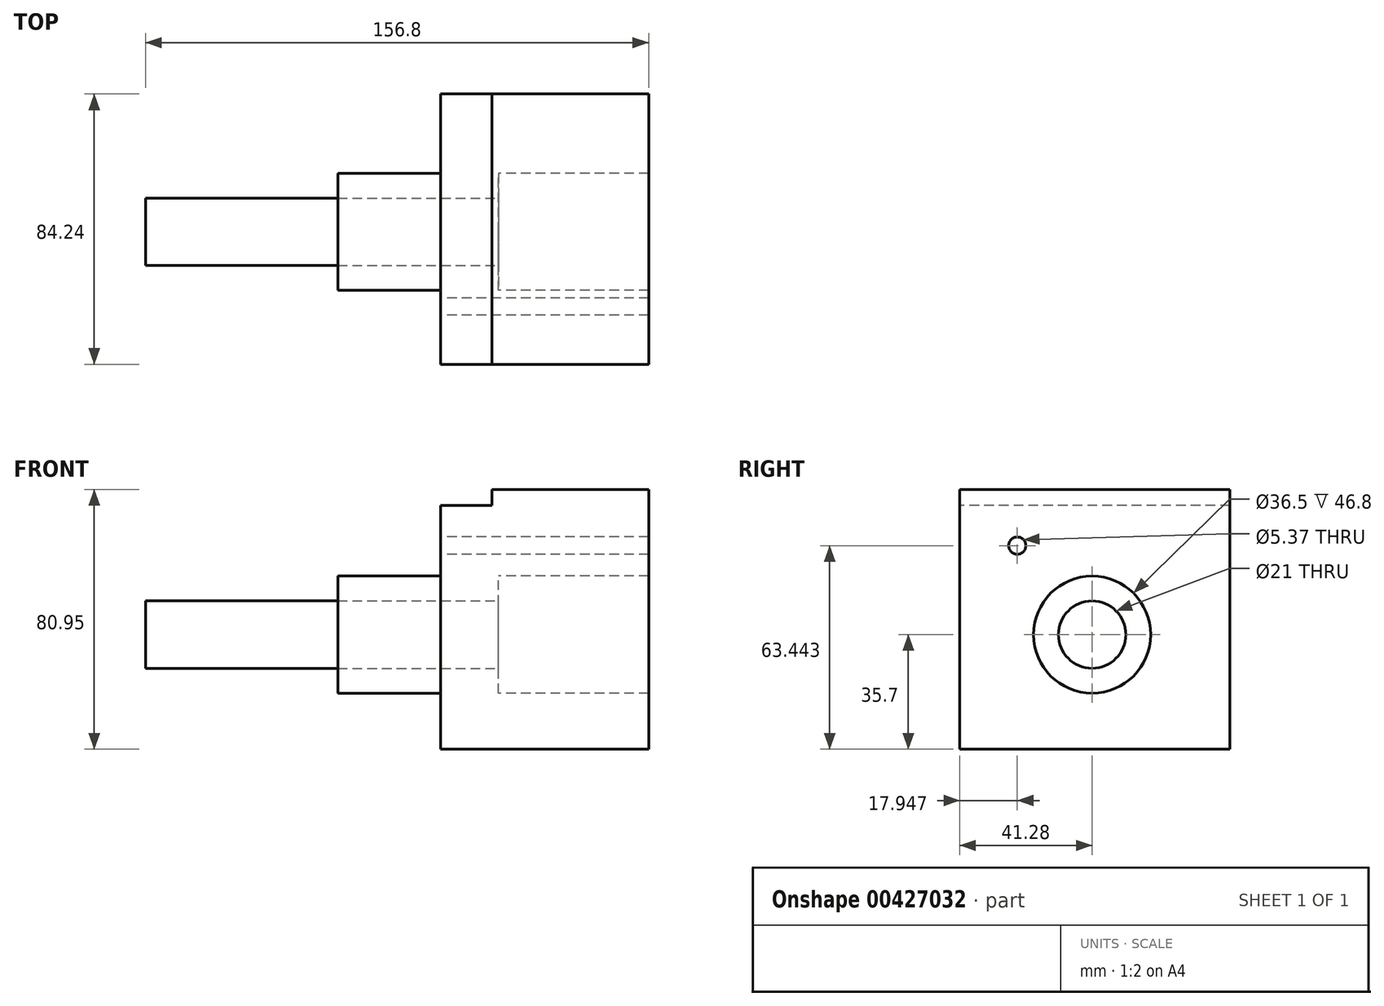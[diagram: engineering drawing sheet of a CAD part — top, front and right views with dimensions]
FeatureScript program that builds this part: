
annotation { "Feature Type Name" : "Feature", "Feature Type Description" : "" }
export const myFeature = defineFeature(function(context is Context, id is Id, definition is map)
    precondition{}
    {
        {
            var Q0;
            Q0=qCreatedBy(makeId("Right.planeOp"),FACE);
            var sketch = newSketch(context, id + "F0", { "sketchPlane" : qUnion([Q0])});
            skCircle(sketch, "E0", {"center": v(0, 0) * mm, "radius": 18.25 * mm});
            skCircle(sketch, "E1", {"center": v(0, 0) * mm, "radius": 10.5 * mm});
            skLineSegment(sketch, "E2.bottom", {"start": v(42.96, 45.25) * mm, "end": v(-41.28, 45.25) * mm});
            skLineSegment(sketch, "E2.top", {"start": v(42.96, -35.7) * mm, "end": v(-41.28, -35.7) * mm});
            skLineSegment(sketch, "E2.left", {"start": v(42.96, 45.25) * mm, "end": v(42.96, -35.7) * mm});
            skLineSegment(sketch, "E2.right", {"start": v(-41.28, 45.25) * mm, "end": v(-41.28, -35.7) * mm});
            skLineSegment(sketch, "E3.top", {"start": v(42.96, 40.25) * mm, "end": v(-41.28, 40.25) * mm});
            skLineSegment(sketch, "E3.left", {"start": v(42.96, 45.25) * mm, "end": v(42.96, 40.25) * mm});
            skLineSegment(sketch, "E3.right", {"start": v(-41.28, 45.25) * mm, "end": v(-41.28, 40.25) * mm});
            skCircle(sketch, "E4", {"center": v(-23.33, 27.74) * mm, "radius": 2.68 * mm});
            skSolve(sketch);
        }
        {
            var Q0;
            Q0=makeQuery(id+"F0.imprint","IMPRINT",FACE,{"disambiguationData":[TD([[makeQuery(id+"F0.imprint","IMPRINT",EDGE,{"derivedFrom":sQuery(id+"F0.wireOp",EDGE,"E0")}),-1.0]])]});
            extrude(context, id + "F1", {"entities" : qUnion([Q0]), "depth" : 64.9 * mm});
        }
        {
            var Q0;
            Q0=makeQuery(id+"F0.imprint","IMPRINT",FACE,{"disambiguationData":[TD([[makeQuery(id+"F0.imprint","IMPRINT",EDGE,{"derivedFrom":sQuery(id+"F0.wireOp",EDGE,"E2.bottom")}),1.0]])]});
            var Q1;
            Q1=makeQuery(id+"F1.opExtrude","CAP_FACE",FACE,{"disambiguationData":[OSD([sQuery(id+"F0.wireOp",EDGE,"E0"),sQuery(id+"F0.wireOp",EDGE,"E2.top"),sQuery(id+"F0.wireOp",EDGE,"E2.left"),sQuery(id+"F0.wireOp",EDGE,"E2.right"),sQuery(id+"F0.wireOp",EDGE,"E3.top"),sQuery(id+"F0.wireOp",EDGE,"E4")])],"isStart":false});
            extrude(context, id + "F2", {"entities" : qUnion([Q0]), "operationType" : NewBodyOperationType.ADD, "endBound" : BoundingType.UP_TO_SURFACE, "endBoundEntityFace" : qUnion([Q1]), "depth" : 69.1 * mm, "hasSecondDirection" : true, "secondDirectionOppositeDirection" : false, "secondDirectionDepth" : 16 * mm});
        }
        {
            var Q0;
            Q0=makeQuery(id+"F0.imprint","IMPRINT",FACE,{"disambiguationData":[TD([[makeQuery(id+"F0.imprint","IMPRINT",EDGE,{"derivedFrom":sQuery(id+"F0.wireOp",EDGE,"E0")}),1.0]])]});
            extrude(context, id + "F3", {"entities" : qUnion([Q0]), "operationType" : NewBodyOperationType.ADD, "oppositeDirection" : true, "depth" : 32 * mm, "hasSecondDirection" : true, "secondDirectionOppositeDirection" : false, "secondDirectionDepth" : 18.1 * mm});
        }
        {
            var Q0;
            Q0=makeQuery(id+"F0.imprint","IMPRINT",FACE,{"disambiguationData":[TD([[makeQuery(id+"F0.imprint","IMPRINT",EDGE,{"derivedFrom":sQuery(id+"F0.wireOp",EDGE,"E1")}),1.0]])]});
            extrude(context, id + "F4", {"entities" : qUnion([Q0]), "oppositeDirection" : true, "depth" : 91.9 * mm});
        }
        {
            var Q0;
            Q0=makeQuery(id+"F3.opExtrude","CAP_FACE",FACE,{"disambiguationData":[OSD([sQuery(id+"F0.wireOp",EDGE,"E0"),sQuery(id+"F0.wireOp",EDGE,"E1")])],"isStart":false});
            cPlane(context, id + "F5", {"entities" : qUnion([Q0]), "cplaneType" : CPlaneType.OFFSET, "offset" : 1 * mm, "width" : 150 * mm, "height" : 150 * mm});
        }
    });
